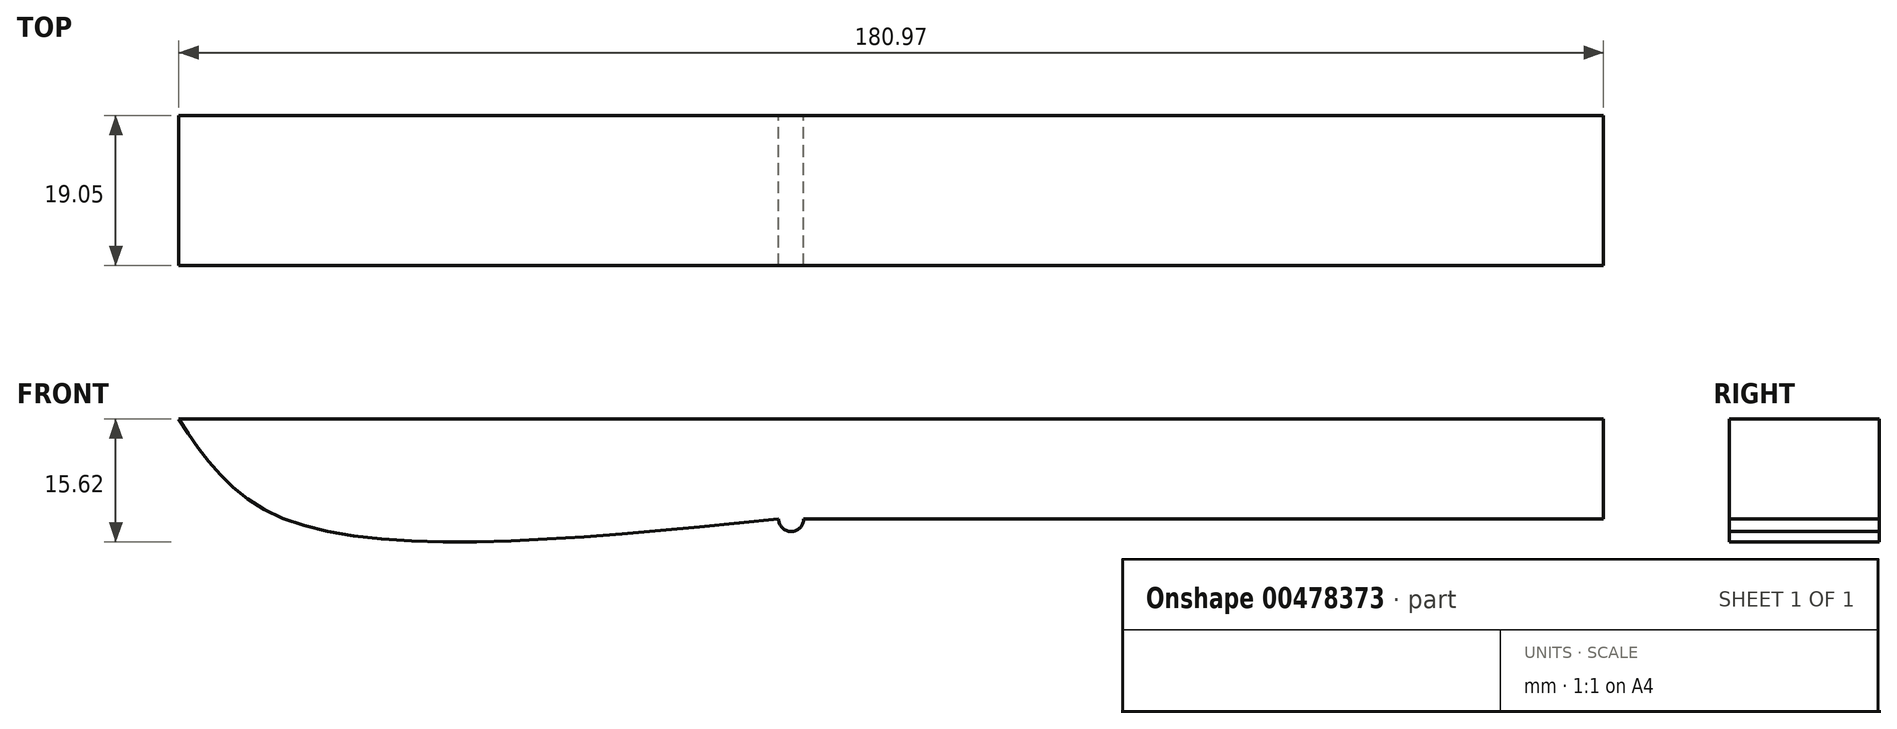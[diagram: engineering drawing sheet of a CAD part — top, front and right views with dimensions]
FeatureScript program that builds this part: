
annotation { "Feature Type Name" : "Feature", "Feature Type Description" : "" }
export const myFeature = defineFeature(function(context is Context, id is Id, definition is map)
    precondition{}
    {
        {
            var Q0;
            Q0=qCreatedBy(makeId("Front.planeOp"),FACE);
            var sketch = newSketch(context, id + "F0", { "sketchPlane" : qUnion([Q0])});
            skLineSegment(sketch, "E0", {"start": v(-32.71, -2.05) * mm, "end": v(43.49, -2.05) * mm});
            skLineSegment(sketch, "E1", {"start": v(43.49, -2.05) * mm, "end": v(46.66, -2.05) * mm});
            skLineSegment(sketch, "E2", {"start": v(46.66, -2.05) * mm, "end": v(148.26, -2.05) * mm});
            skLineSegment(sketch, "E3", {"start": v(43.49, -2.05) * mm, "end": v(43.49, -14.75) * mm});
            skFitSpline(sketch, "E4", {"points": [v(-32.71, -2.05) * mm, v(-19.27, -14.75) * mm, v(43.49, -14.75) * mm], "startDerivative": vector(27.88, -42.45) * mm, "endDerivative": vector(115.83, 11.7) * mm});
            skLineSegment(sketch, "E5", {"start": v(43.49, -14.75) * mm, "end": v(148.26, -14.75) * mm});
            skLineSegment(sketch, "E6", {"start": v(148.26, -14.75) * mm, "end": v(148.26, -2.05) * mm});
            skLineSegment(sketch, "E7", {"start": v(46.66, -14.75) * mm, "end": v(46.66, -2.05) * mm});
            skArc(sketch, "E8", {"start": v(43.49, -14.75) * mm, "mid": v(45.08, -16.34) * mm, "end": v(46.66, -14.75) * mm});
            skSolve(sketch);
        }
        {
            var Q0;
            Q0 = qSketchRegion(id + "F0", true);
            extrude(context, id + "F1", {"entities" : qUnion([Q0]), "depth" : 19.05 * mm});
        }
    });
